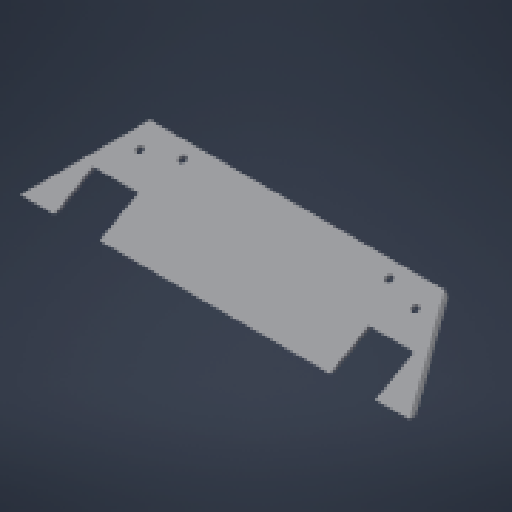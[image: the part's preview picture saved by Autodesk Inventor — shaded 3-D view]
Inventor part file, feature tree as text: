
AUTODESK INVENTOR PART (.ipt)
format: ipt  version: 2023 (Build 270158000, 158)  size: 164,864 bytes
history: native  units: mm
features: extrude x3, sketch x3, other x1
ambient origin geometry x8: Origin, YZ Plane, XZ Plane, XY Plane, X Axis, Y Axis, Z Axis, Center Point
bodies: Body1 (feature_tree)
feature tree (7):
  other  "Bryła1"
  extrude  "Wyciągnięcie proste1"  Depth=1.5mm
  extrude  "Wyciągnięcie proste2"  Depth=22.0mm
  extrude  "Wyciągnięcie proste3"  TaperAngle=30.0deg  [1 undecoded]
  sketch  "Szkic1"
  sketch  "Szkic2"
  sketch  "Szkic3"
note: 1 required parameter value undecoded (feature->parameter linkage not recoverable at this tier; creation-order binding heuristic only, values carry confidence <= 0.55)
